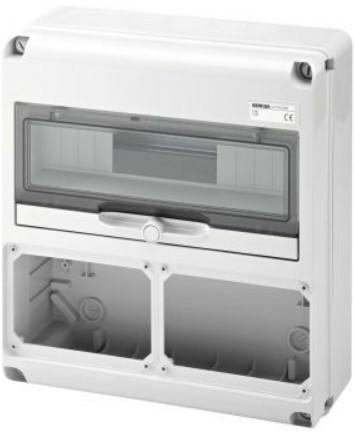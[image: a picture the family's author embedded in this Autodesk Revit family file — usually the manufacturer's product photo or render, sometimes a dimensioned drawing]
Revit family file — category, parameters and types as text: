
# Revit family: Building-QuadriIEC309-GEWISS-68QDIN-QUADRI-PRESE-14MOD_2PRESE_IB_ORIZ
name_source: partatom
category: Apparecchi elettrici
units: mm (PartAtom-declared; Revit-internal decimal feet)

## family parameters
Condiviso = No
Host = Superficie
Mantenere orientamento annotazione = Sì
Punto di calcolo locali = Sì
Quota connettore circolare = Usa diametro
Taglio con vuoti quando caricato = No
Tipo di parte = Normale

## types (1)
- GW68006N - Q-DIN 14M 2FLANGE PR.BL.OR.SBF IP65
    Catalogo = BUILDING
    Catalogo Serie = 68 QDIN
    Classe isolamento = II
    Codice EAN = 8011564744776
    Codice Electrocod = 2242
    Colore = Grigio RAL 7035
    Conformità normativa = EN 60208 - EN 60670-1 - IEC 60670-24
    Descrizione = Q-DIN 14M 2FLANGE PR.BL.OR.SBF IP65
    Glow Wire Test = 650°C
    Grado di protezione = IP65
    IDF = 9171d5b0-c39f-4c93-a937-604f849fb133
    IDT = 025e6d85-348f-4064-8737-2dc7c756130e
    Immagine tipo = GW68006N.jpg
    Modello = GW68006N
    N. IEC 309/IB alloggiabili = 2 IB Orizz. 16/32 A SBF IP44 affiancate
    N. coperchi ciechi in dotazione = 1 IB 16/32 A
    N. flange in dotazione = 1 IB 16/32 A
    N. mod. EN 50022 = 14
    N. prese IB alloggiabili: = 2 IB Orizz. 16/32 A SBF IP44 affiancate
    N. prese alloggiabili = 2 IB Orizz. 16/32 A SBF IP44 affiancate
    POMELLO = bianco
    PRESA = rosso
    Potenza dissipabile A (W) = 24
    Potenza dissipabile B (W) = 64
    Produttore = GEWISS S.p.A.
    Prospetto di default = 1219 mm
    Resistenza agli urti = IK08
    SEO = Quadretto
    STRUTTURA = RAL - 7035
    STRUTTURA ALTA = Poche
    Scheda Tecnica = https://www.gewiss.com
    Spostamento_S = 1000 mm  [stored 3.28084 ft]
    Temperatura di funzionamento = -25 ÷ +40 °C
    Temperatura di utilizzo = -25 +40 °C
    Termopressione con biglia = 70 °C
    Tipo versione = Vuoto
    Tipologia di installazione = Da parete
    URL = https://www.gewiss.com
    VETRO = Vetro
    Versione file RFA = 21.5

note: [stored X ft] marks values corroborated as IEEE doubles in the binary element streams (Revit-internal decimal feet)

## geometry (parser evidence)
native form markers: Sweep x3
no freeform markers — native parametric forms only
